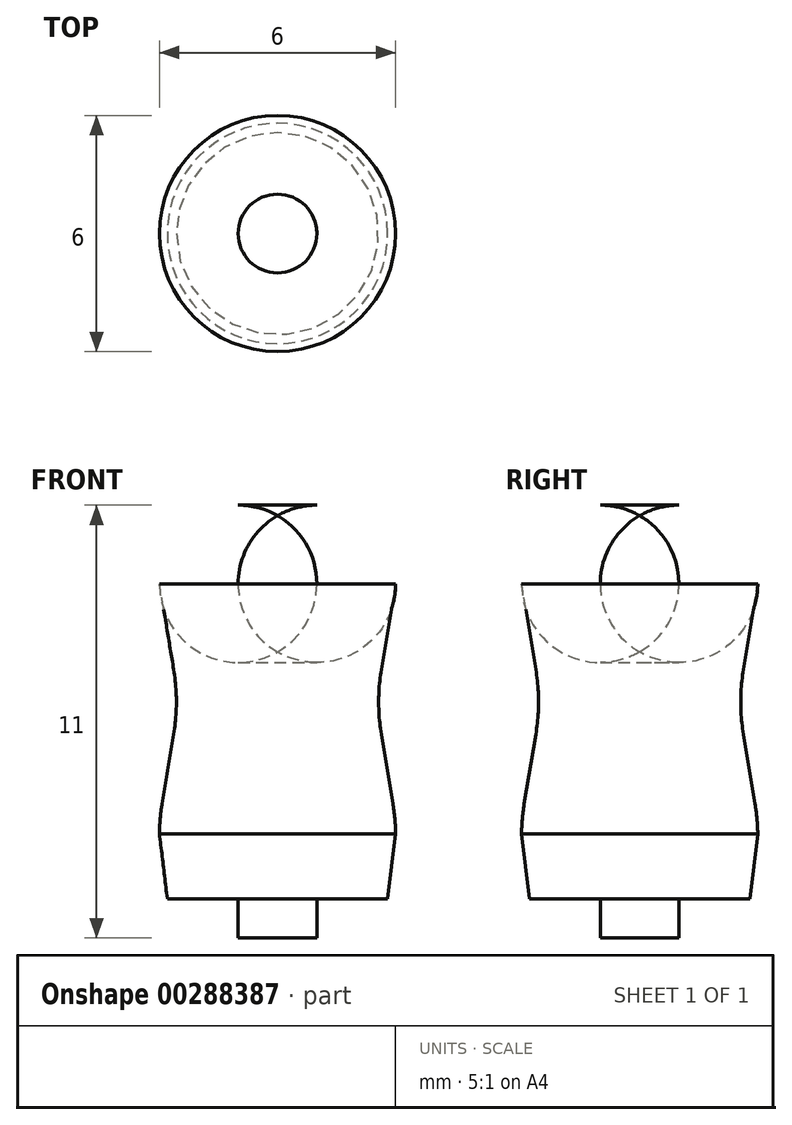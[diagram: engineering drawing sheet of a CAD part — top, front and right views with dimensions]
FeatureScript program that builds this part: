
annotation { "Feature Type Name" : "Feature", "Feature Type Description" : "" }
export const myFeature = defineFeature(function(context is Context, id is Id, definition is map)
    precondition{}
    {
        {
            var Q0;
            Q0=qCreatedBy(makeId("Front.planeOp"),FACE);
            var sketch = newSketch(context, id + "F0", { "sketchPlane" : qUnion([Q0])});
            skLineSegment(sketch, "E0", {"start": v(-7.57, 0) * mm, "end": v(2.8, 0) * mm, "construction": true});
            skLineSegment(sketch, "E1", {"start": v(0, -5.92) * mm, "end": v(0, 10) * mm, "construction": true});
            skLineSegment(sketch, "E2", {"start": v(2.93, 2.4) * mm, "end": v(2.64, 4.18) * mm});
            skLineSegment(sketch, "E3", {"start": v(2.64, 5.82) * mm, "end": v(3, 8) * mm});
            skLineSegment(sketch, "E4", {"start": v(1, 10) * mm, "end": v(0, 10) * mm});
            skLineSegment(sketch, "E5", {"start": v(2.5, 5) * mm, "end": v(-2.5, 5) * mm, "construction": true});
            skPoint(sketch, "E6", {"position": v(0, 5) * mm});
            skPoint(sketch, "E7.visualSharp", {"position": v(2.5, 5) * mm});
            skArc(sketch, "E7.filletArc", {"start": v(2.64, 5.82) * mm, "mid": v(2.57, 5) * mm, "end": v(2.64, 4.18) * mm});
            skPoint(sketch, "E8.visualSharp", {"position": v(3, 8) * mm});
            skLineSegment(sketch, "E8.filletArc", {"start": v(3, 8) * mm, "end": v(3, 8) * mm});
            skPoint(sketch, "E9.visualSharp", {"position": v(3, 2) * mm});
            skArc(sketch, "E9.filletArc", {"start": v(3, 1.65) * mm, "mid": v(2.98, 2.03) * mm, "end": v(2.93, 2.4) * mm});
            skPoint(sketch, "E10.visualSharp", {"position": v(3, 10) * mm});
            skArc(sketch, "E10.filletArc", {"start": v(3, 8) * mm, "mid": v(2.41, 9.41) * mm, "end": v(1, 10) * mm});
            skLineSegment(sketch, "E11", {"start": v(0, 0) * mm, "end": v(0, -1) * mm});
            skLineSegment(sketch, "E12", {"start": v(0, -1) * mm, "end": v(1, -1) * mm});
            skLineSegment(sketch, "E13", {"start": v(1, -1) * mm, "end": v(1, 0) * mm});
            skLineSegment(sketch, "E14", {"start": v(0, -1) * mm, "end": v(0, 10) * mm});
            skLineSegment(sketch, "E15", {"start": v(1, 0) * mm, "end": v(2.8, 0) * mm});
            skLineSegment(sketch, "E16", {"start": v(2.8, 0) * mm, "end": v(3, 1.65) * mm});
            skSolve(sketch);
        }
        {
            var Q0;
            Q0 = qSketchRegion(id + "F0", true);
            var Q1;
            Q1=sQuery(id+"F0.wireOp",EDGE,"E14");
            revolve(context, id + "F1", {"entities" : qUnion([Q0]), "axis" : qUnion([Q1]), "revolveType" : RevolveType.FULL});
        }
    });
